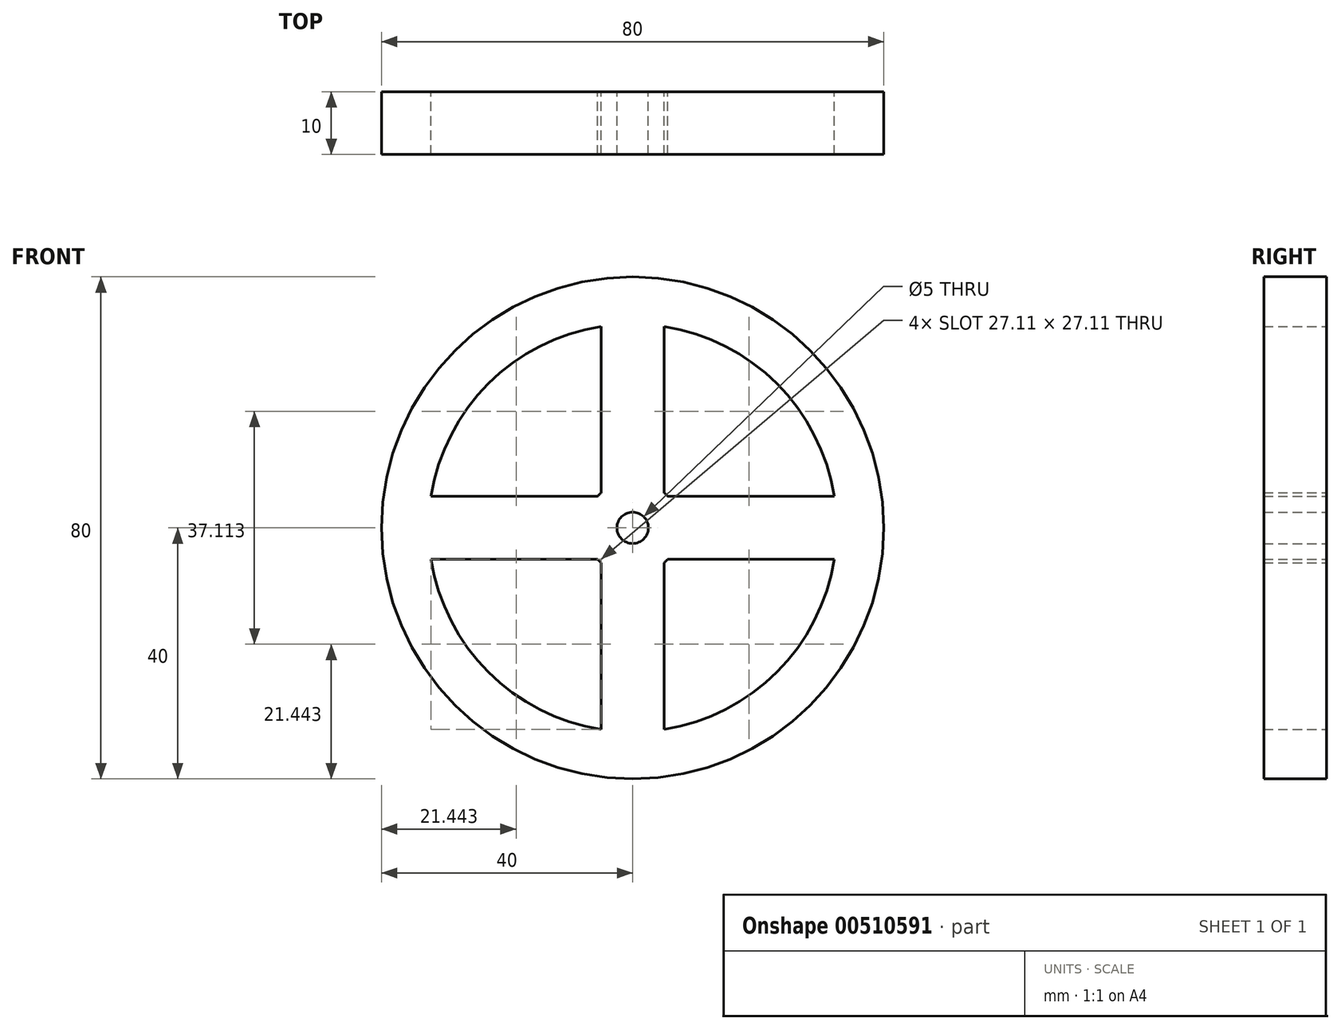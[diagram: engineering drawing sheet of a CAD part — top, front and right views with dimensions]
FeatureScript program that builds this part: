
annotation { "Feature Type Name" : "Feature", "Feature Type Description" : "" }
export const myFeature = defineFeature(function(context is Context, id is Id, definition is map)
    precondition{}
    {
        {
            var Q0;
            Q0=qCreatedBy(makeId("Front.planeOp"),FACE);
            var sketch = newSketch(context, id + "F0", { "sketchPlane" : qUnion([Q0])});
            skArc(sketch, "E0", {"start": v(-5, 32.11) * mm, "mid": v(-22.98, 22.98) * mm, "end": v(-32.11, 5) * mm});
            skCircle(sketch, "E1", {"center": v(0, 0) * mm, "radius": 40 * mm});
            skArc(sketch, "E2", {"start": v(5.6, 5) * mm, "mid": v(5.3, 5.3) * mm, "end": v(5, 5.6) * mm});
            skCircle(sketch, "E3", {"center": v(0, 0) * mm, "radius": 2.5 * mm});
            skLineSegment(sketch, "E4.0", {"start": v(-5, -5.6) * mm, "end": v(-5, -32.11) * mm});
            skLineSegment(sketch, "E5.0", {"start": v(5, -5.6) * mm, "end": v(5, -32.11) * mm});
            skLineSegment(sketch, "E6.0", {"start": v(5.6, -5) * mm, "end": v(32.11, -5) * mm});
            skLineSegment(sketch, "E7.0", {"start": v(5.6, 5) * mm, "end": v(32.11, 5) * mm});
            skLineSegment(sketch, "E8.0", {"start": v(-5.6, 5) * mm, "end": v(-32.11, 5) * mm});
            skLineSegment(sketch, "E9.0", {"start": v(-5.6, -5) * mm, "end": v(-32.11, -5) * mm});
            skPoint(sketch, "E10.orphan", {"position": v(0, 40) * mm});
            skArc(sketch, "E11.trimOffspring", {"start": v(-5, 5.6) * mm, "mid": v(-5.3, 5.3) * mm, "end": v(-5.6, 5) * mm});
            skArc(sketch, "E12.trimOffspring", {"start": v(-5.6, -5) * mm, "mid": v(-5.3, -5.3) * mm, "end": v(-5, -5.6) * mm});
            skArc(sketch, "E13.trimOffspring", {"start": v(5, -5.6) * mm, "mid": v(5.3, -5.3) * mm, "end": v(5.6, -5) * mm});
            skArc(sketch, "E14.trimOffspring", {"start": v(-32.11, -5) * mm, "mid": v(-22.98, -22.98) * mm, "end": v(-5, -32.11) * mm});
            skLineSegment(sketch, "E15.trimOffspring", {"start": v(-5, 32.11) * mm, "end": v(-5, 5.6) * mm});
            skLineSegment(sketch, "E16.trimOffspring", {"start": v(5, 32.11) * mm, "end": v(5, 5.6) * mm});
            skArc(sketch, "E17.trimOffspring", {"start": v(5, -32.11) * mm, "mid": v(32.5, 0) * mm, "end": v(5, 32.11) * mm});
            skSolve(sketch);
        }
        {
            var Q0;
            Q0=makeQuery(id+"F0.imprint","IMPRINT",FACE,{"disambiguationData":[TD([[makeQuery(id+"F0.imprint","IMPRINT",EDGE,{"derivedFrom":sQuery(id+"F0.wireOp",EDGE,"E0")}),-1.0]])]});
            extrude(context, id + "F1", {"entities" : qUnion([Q0]), "depth" : 10 * mm, "offsetDistance" : 25 * mm});
        }
    });
